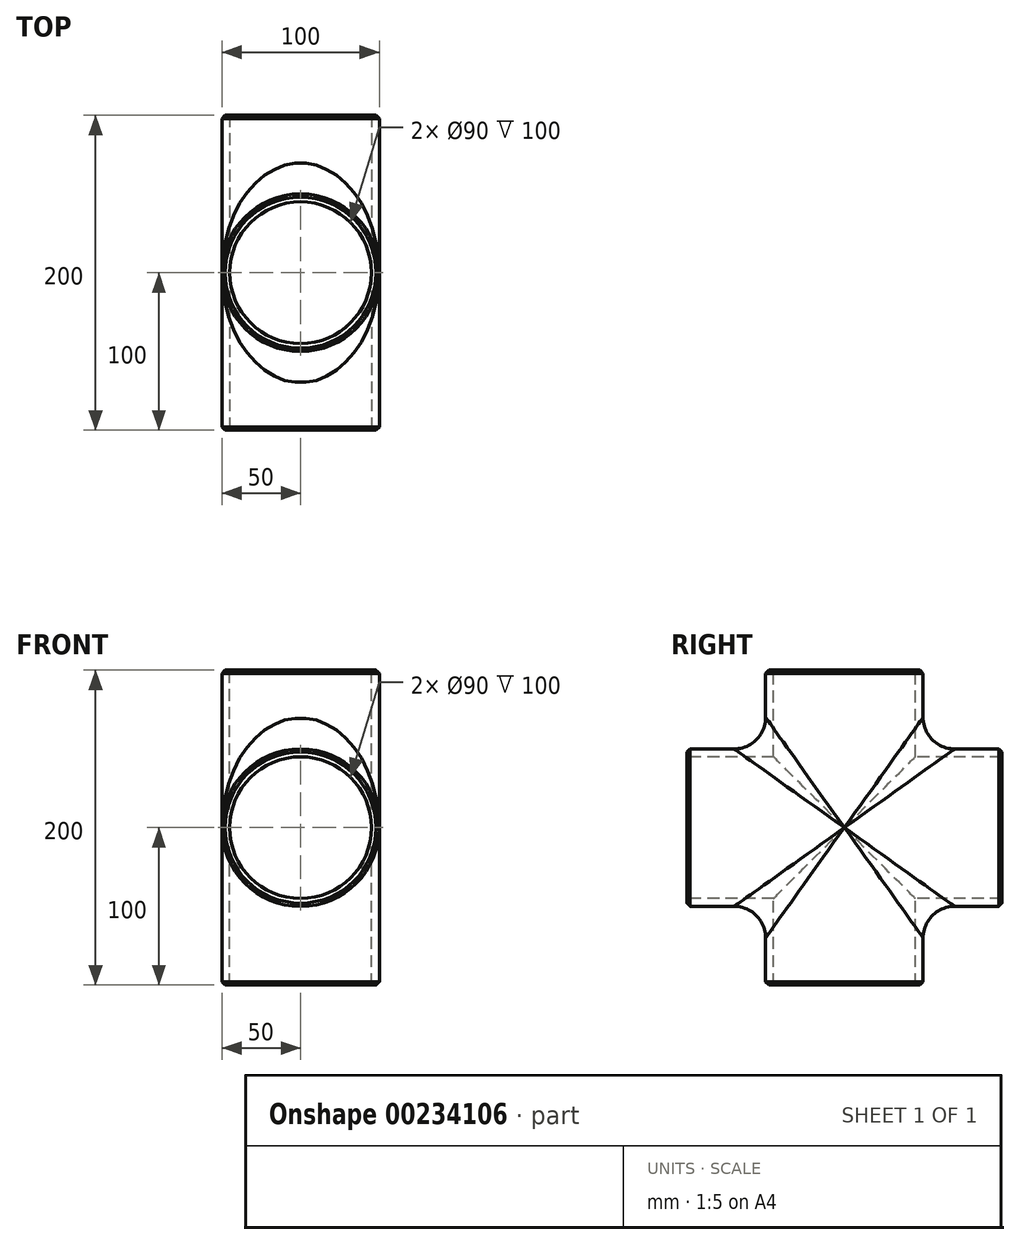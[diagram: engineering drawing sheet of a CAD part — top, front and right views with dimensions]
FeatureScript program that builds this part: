
annotation { "Feature Type Name" : "Feature", "Feature Type Description" : "" }
export const myFeature = defineFeature(function(context is Context, id is Id, definition is map)
    precondition{}
    {
        {
            var Q0;
            Q0=qCreatedBy(makeId("Front.planeOp"),FACE);
            var sketch = newSketch(context, id + "F0", { "sketchPlane" : qUnion([Q0])});
            skCircle(sketch, "E0", {"center": v(0, 0) * mm, "radius": 50 * mm});
            skSolve(sketch);
        }
        {
            var Q0;
            Q0 = qSketchRegion(id + "F0", true);
            extrude(context, id + "F1", {"entities" : qUnion([Q0]), "depth" : 100 * mm});
        }
        {
            var Q0;
            Q0=makeQuery(id+"F1.opExtrude","CAP_FACE",FACE,{"disambiguationData":[OSD([sQuery(id+"F0.wireOp",EDGE,"E0")])],"isStart":true});
            extrude(context, id + "F2", {"entities" : qUnion([Q0]), "operationType" : NewBodyOperationType.ADD, "depth" : 100 * mm});
        }
        {
            var Q0;
            Q0=qCreatedBy(makeId("Top.planeOp"),FACE);
            var sketch = newSketch(context, id + "F3", { "sketchPlane" : qUnion([Q0])});
            skCircle(sketch, "E1", {"center": v(0, 0) * mm, "radius": 50 * mm});
            skSolve(sketch);
        }
        {
            var Q0;
            Q0 = qSketchRegion(id + "F3", true);
            extrude(context, id + "F4", {"entities" : qUnion([Q0]), "operationType" : NewBodyOperationType.ADD, "depth" : 100 * mm});
        }
        {
            var Q0;
            Q0=qCreatedBy(makeId("Top.planeOp"),FACE);
            var sketch = newSketch(context, id + "F5", { "sketchPlane" : qUnion([Q0])});
            skCircle(sketch, "E2", {"center": v(0, 0) * mm, "radius": 40 * mm});
            skSolve(sketch);
        }
        {
            var Q0;
            Q0 = qSketchRegion(id + "F5", true);
            extrude(context, id + "F6", {"entities" : qUnion([Q0]), "operationType" : NewBodyOperationType.ADD, "depth" : 100 * mm});
        }
        {
            var Q0;
            Q0=makeQuery(id+"F4.opExtrude","CAP_FACE",FACE,{"disambiguationData":[OSD([sQuery(id+"F3.wireOp",EDGE,"E1")])],"isStart":false});
            extrude(context, id + "F7", {"entities" : qUnion([Q0]), "operationType" : NewBodyOperationType.ADD, "oppositeDirection" : true, "depth" : 200 * mm});
        }
        {
            var Q0;
            Q0=makeQuery(id+"F1.opExtrude","CAP_FACE",FACE,{"disambiguationData":[OSD([sQuery(id+"F0.wireOp",EDGE,"E0")])],"isStart":false});
            var sketch = newSketch(context, id + "F8", { "sketchPlane" : qUnion([Q0])});
            skCircle(sketch, "E3", {"center": v(0, 0) * mm, "radius": 45 * mm});
            skSolve(sketch);
        }
        {
            var Q0;
            Q0 = qSketchRegion(id + "F8", true);
            extrude(context, id + "F9", {"entities" : qUnion([Q0]), "operationType" : NewBodyOperationType.REMOVE, "oppositeDirection" : true, "depth" : 200 * mm});
        }
        {
            var Q0;
            Q0=makeQuery(id+"F4.opExtrude","CAP_FACE",FACE,{"disambiguationData":[OSD([sQuery(id+"F3.wireOp",EDGE,"E1")])],"isStart":false});
            var sketch = newSketch(context, id + "F10", { "sketchPlane" : qUnion([Q0])});
            skCircle(sketch, "E4", {"center": v(0, 0) * mm, "radius": 45 * mm});
            skSolve(sketch);
        }
        {
            var Q0;
            Q0 = qSketchRegion(id + "F10", true);
            extrude(context, id + "F11", {"entities" : qUnion([Q0]), "operationType" : NewBodyOperationType.REMOVE, "oppositeDirection" : true, "depth" : 200 * mm});
        }
        {
            var Q0;
            {var subQ0=sQuery(id+"F0.wireOp",EDGE,"E0");Q0=makeQuery(id+"F4.boolean.opBoolean","INTERSECT",EDGE,{"disambiguationData":[OD(1.0)],"derivedFrom":[makeQuery(id+"F2.boolean.opBoolean","MERGE",FACE,{"derivedFrom":[makeQuery(id+"F1.opExtrude","SWEPT_FACE",FACE,{"disambiguationData":[OSD([subQ0])]}),makeQuery(id+"F2.opExtrude","SWEPT_FACE",FACE,{"disambiguationData":[OSD([subQ0])]})]}),makeQuery(id+"F4.opExtrude","SWEPT_FACE",FACE,{"disambiguationData":[OSD([sQuery(id+"F3.wireOp",EDGE,"E1")])]})]});}
            var Q1;
            {var subQ0=sQuery(id+"F0.wireOp",EDGE,"E0");Q1=makeQuery(id+"F4.boolean.opBoolean","INTERSECT",EDGE,{"disambiguationData":[OD(0.0)],"derivedFrom":[makeQuery(id+"F2.boolean.opBoolean","MERGE",FACE,{"derivedFrom":[makeQuery(id+"F1.opExtrude","SWEPT_FACE",FACE,{"disambiguationData":[OSD([subQ0])]}),makeQuery(id+"F2.opExtrude","SWEPT_FACE",FACE,{"disambiguationData":[OSD([subQ0])]})]}),makeQuery(id+"F4.opExtrude","SWEPT_FACE",FACE,{"disambiguationData":[OSD([sQuery(id+"F3.wireOp",EDGE,"E1")])]})]});}
            var Q2;
            {var subQ0=sQuery(id+"F0.wireOp",EDGE,"E0");Q2=makeQuery(id+"F7.boolean.opBoolean","INTERSECT",EDGE,{"disambiguationData":[OD(0.0)],"derivedFrom":[makeQuery(id+"F2.boolean.opBoolean","MERGE",FACE,{"derivedFrom":[makeQuery(id+"F1.opExtrude","SWEPT_FACE",FACE,{"disambiguationData":[OSD([subQ0])]}),makeQuery(id+"F2.opExtrude","SWEPT_FACE",FACE,{"disambiguationData":[OSD([subQ0])]})]}),makeQuery(id+"F7.opExtrude","SWEPT_FACE",FACE,{"disambiguationData":[OSD([sQuery(id+"F3.wireOp",EDGE,"E1")])]})]});}
            var Q3;
            {var subQ0=sQuery(id+"F0.wireOp",EDGE,"E0");Q3=makeQuery(id+"F7.boolean.opBoolean","INTERSECT",EDGE,{"disambiguationData":[OD(1.0)],"derivedFrom":[makeQuery(id+"F2.boolean.opBoolean","MERGE",FACE,{"derivedFrom":[makeQuery(id+"F1.opExtrude","SWEPT_FACE",FACE,{"disambiguationData":[OSD([subQ0])]}),makeQuery(id+"F2.opExtrude","SWEPT_FACE",FACE,{"disambiguationData":[OSD([subQ0])]})]}),makeQuery(id+"F7.opExtrude","SWEPT_FACE",FACE,{"disambiguationData":[OSD([sQuery(id+"F3.wireOp",EDGE,"E1")])]})]});}
            fillet(context, id + "F12", {"entities" : qUnion([Q0, Q1, Q2, Q3]), "radius" : 20 * mm, "tangentPropagation" : true, "allowEdgeOverflow" : false});
        }
        {
            var Q0;
            Q0=makeQuery(id+"F1.opExtrude","CAP_EDGE",EDGE,{"disambiguationData":[OSD([sQuery(id+"F0.wireOp",EDGE,"E0")])],"isStart":false});
            var Q1;
            Q1=makeQuery(id+"F7.opExtrude","CAP_EDGE",EDGE,{"disambiguationData":[OSD([sQuery(id+"F3.wireOp",EDGE,"E1")])],"isStart":false});
            var Q2;
            Q2=makeQuery(id+"F2.opExtrude","CAP_EDGE",EDGE,{"disambiguationData":[OSD([sQuery(id+"F0.wireOp",EDGE,"E0")])],"isStart":false});
            var Q3;
            Q3=makeQuery(id+"F4.opExtrude","CAP_EDGE",EDGE,{"disambiguationData":[OSD([sQuery(id+"F3.wireOp",EDGE,"E1")])],"isStart":false});
            chamfer(context, id + "F13", {"entities" : qUnion([Q0, Q1, Q2, Q3]), "width" : 2 * mm, "tangentPropagation" : true});
        }
    });
